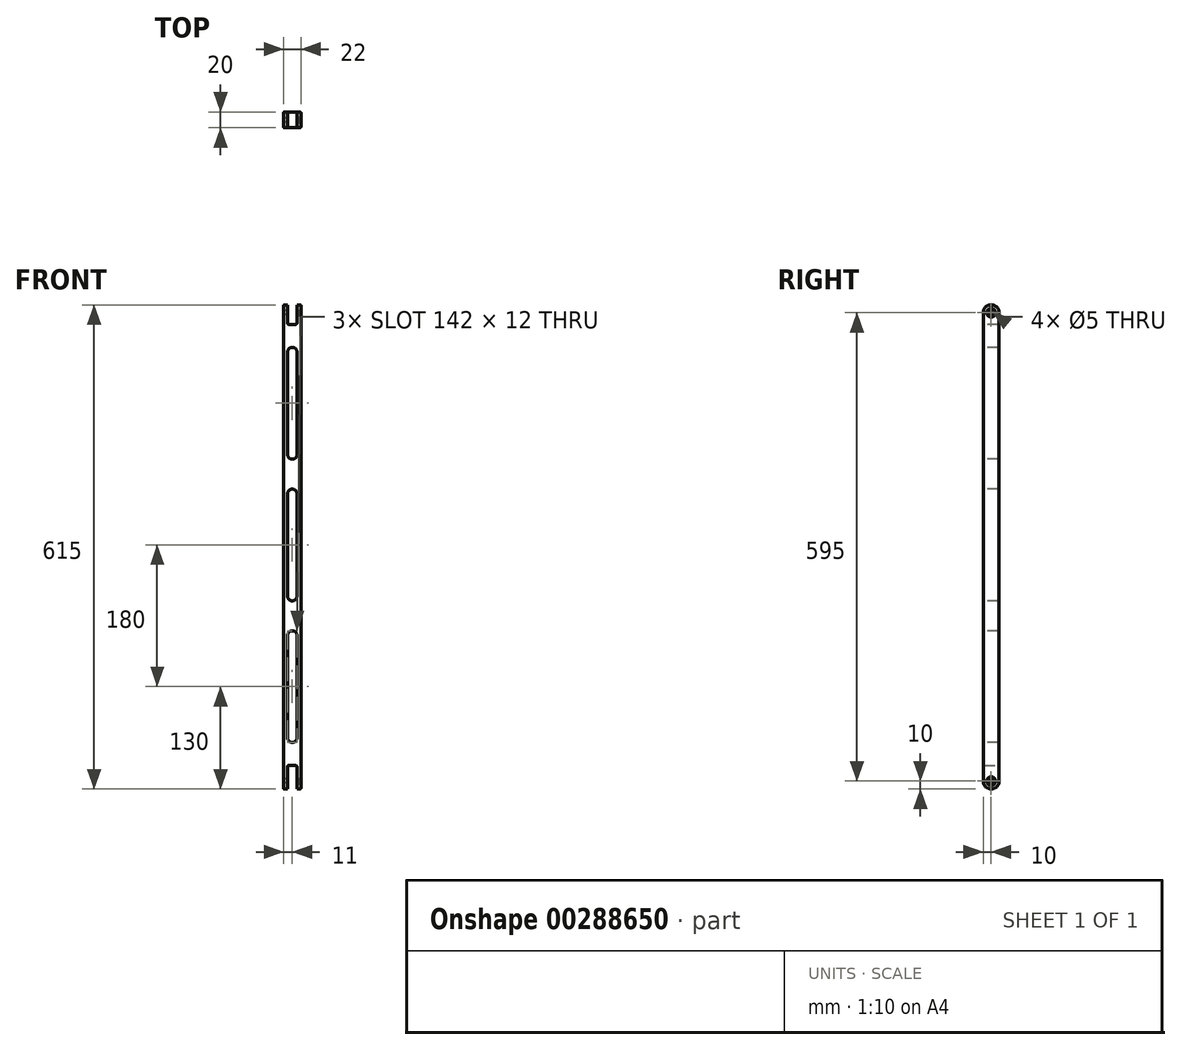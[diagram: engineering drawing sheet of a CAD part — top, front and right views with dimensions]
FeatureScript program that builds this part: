
annotation { "Feature Type Name" : "Feature", "Feature Type Description" : "" }
export const myFeature = defineFeature(function(context is Context, id is Id, definition is map)
    precondition{}
    {
        {
            var Q0;
            Q0=qCreatedBy(makeId("Front.planeOp"),FACE);
            var sketch = newSketch(context, id + "F0", { "sketchPlane" : qUnion([Q0])});
            skLineSegment(sketch, "E0.bottom", {"start": v(11, 307.5) * mm, "end": v(-11, 307.5) * mm});
            skLineSegment(sketch, "E0.top", {"start": v(11, -307.5) * mm, "end": v(-11, -307.5) * mm});
            skLineSegment(sketch, "E0.left", {"start": v(11, 307.5) * mm, "end": v(11, -307.5) * mm});
            skLineSegment(sketch, "E0.right", {"start": v(-11, 307.5) * mm, "end": v(-11, -307.5) * mm});
            skPoint(sketch, "E0.middle", {"position": v(0, 0) * mm});
            skSolve(sketch);
        }
        {
            var Q0;
            Q0=makeQuery(id+"F0.imprint","IMPRINT",FACE,{"disambiguationData":[TD([[makeQuery(id+"F0.imprint","IMPRINT",EDGE,{"derivedFrom":sQuery(id+"F0.wireOp",EDGE,"E0.bottom")}),1.0]])]});
            extrude(context, id + "F1", {"entities" : qUnion([Q0]), "depth" : 20 * mm});
        }
        {
            var Q0;
            Q0=makeQuery(id+"F1.opExtrude","SWEPT_FACE",FACE,{"disambiguationData":[OSD([sQuery(id+"F0.wireOp",EDGE,"E0.bottom")])]});
            var sketch = newSketch(context, id + "F2", { "sketchPlane" : qUnion([Q0])});
            skLineSegment(sketch, "E1.bottom", {"start": v(-6, 0) * mm, "end": v(6, 0) * mm});
            skLineSegment(sketch, "E1.top", {"start": v(-6, -20) * mm, "end": v(6, -20) * mm});
            skLineSegment(sketch, "E1.left", {"start": v(-6, 0) * mm, "end": v(-6, -20) * mm});
            skLineSegment(sketch, "E1.right", {"start": v(6, 0) * mm, "end": v(6, -20) * mm});
            skSolve(sketch);
        }
        {
            var Q0;
            Q0=makeQuery(id+"F2.imprint","IMPRINT",FACE,{"disambiguationData":[TD([[makeQuery(id+"F2.imprint","IMPRINT",EDGE,{"derivedFrom":sQuery(id+"F2.wireOp",EDGE,"E1.bottom")}),1.0]])]});
            extrude(context, id + "F3", {"entities" : qUnion([Q0]), "operationType" : NewBodyOperationType.REMOVE, "oppositeDirection" : true, "depth" : 25 * mm});
        }
        {
            var Q0;
            Q0=makeQuery(id+"F1.opExtrude","SWEPT_FACE",FACE,{"disambiguationData":[OSD([sQuery(id+"F0.wireOp",EDGE,"E0.top")])]});
            var sketch = newSketch(context, id + "F4", { "sketchPlane" : qUnion([Q0])});
            skLineSegment(sketch, "E2.bottom", {"start": v(-6, 20) * mm, "end": v(6, 20) * mm});
            skLineSegment(sketch, "E2.top", {"start": v(-6, 0) * mm, "end": v(6, 0) * mm});
            skLineSegment(sketch, "E2.left", {"start": v(-6, 20) * mm, "end": v(-6, 0) * mm});
            skLineSegment(sketch, "E2.right", {"start": v(6, 20) * mm, "end": v(6, 0) * mm});
            skSolve(sketch);
        }
        {
            var Q0;
            Q0=makeQuery(id+"F4.imprint","IMPRINT",FACE,{"disambiguationData":[TD([[makeQuery(id+"F4.imprint","IMPRINT",EDGE,{"derivedFrom":sQuery(id+"F4.wireOp",EDGE,"E2.bottom")}),1.0]])]});
            extrude(context, id + "F5", {"entities" : qUnion([Q0]), "operationType" : NewBodyOperationType.REMOVE, "oppositeDirection" : true, "depth" : 30 * mm});
        }
        {
            var Q0;
            {var subQ0=sQuery(id+"F0.wireOp",EDGE,"E0.right");var subQ1=sQuery(id+"F0.wireOp",EDGE,"E0.top");Q0=makeQuery(id+"F5.boolean.opBoolean","SPLIT",EDGE,{"disambiguationData":[TD([makeQuery(id+"F1.opExtrude","SWEPT_FACE",FACE,{"disambiguationData":[OSD([subQ0])]})])],"derivedFrom":makeQuery(id+"F1.opExtrude","CAP_EDGE",EDGE,{"disambiguationData":[OSD([subQ1])],"isStart":true})});}
            var Q1;
            {var subQ0=sQuery(id+"F0.wireOp",EDGE,"E0.left");var subQ1=sQuery(id+"F0.wireOp",EDGE,"E0.top");Q1=makeQuery(id+"F5.boolean.opBoolean","SPLIT",EDGE,{"disambiguationData":[TD([makeQuery(id+"F1.opExtrude","SWEPT_FACE",FACE,{"disambiguationData":[OSD([subQ0])]})])],"derivedFrom":makeQuery(id+"F1.opExtrude","CAP_EDGE",EDGE,{"disambiguationData":[OSD([subQ1])],"isStart":true})});}
            var Q2;
            {var subQ0=sQuery(id+"F0.wireOp",EDGE,"E0.left");var subQ1=sQuery(id+"F0.wireOp",EDGE,"E0.top");Q2=makeQuery(id+"F5.boolean.opBoolean","SPLIT",EDGE,{"disambiguationData":[TD([makeQuery(id+"F1.opExtrude","SWEPT_FACE",FACE,{"disambiguationData":[OSD([subQ0])]})])],"derivedFrom":makeQuery(id+"F1.opExtrude","CAP_EDGE",EDGE,{"disambiguationData":[OSD([subQ1])],"isStart":false})});}
            var Q3;
            {var subQ0=sQuery(id+"F0.wireOp",EDGE,"E0.right");var subQ1=sQuery(id+"F0.wireOp",EDGE,"E0.top");Q3=makeQuery(id+"F5.boolean.opBoolean","SPLIT",EDGE,{"disambiguationData":[TD([makeQuery(id+"F1.opExtrude","SWEPT_FACE",FACE,{"disambiguationData":[OSD([subQ0])]})])],"derivedFrom":makeQuery(id+"F1.opExtrude","CAP_EDGE",EDGE,{"disambiguationData":[OSD([subQ1])],"isStart":false})});}
            var Q4;
            {var subQ0=sQuery(id+"F0.wireOp",EDGE,"E0.bottom");var subQ1=sQuery(id+"F0.wireOp",EDGE,"E0.right");Q4=makeQuery(id+"F3.boolean.opBoolean","SPLIT",EDGE,{"disambiguationData":[TD([makeQuery(id+"F1.opExtrude","SWEPT_FACE",FACE,{"disambiguationData":[OSD([subQ1])]})])],"derivedFrom":makeQuery(id+"F1.opExtrude","CAP_EDGE",EDGE,{"disambiguationData":[OSD([subQ0])],"isStart":false})});}
            var Q5;
            {var subQ0=sQuery(id+"F0.wireOp",EDGE,"E0.bottom");var subQ1=sQuery(id+"F0.wireOp",EDGE,"E0.right");Q5=makeQuery(id+"F3.boolean.opBoolean","SPLIT",EDGE,{"disambiguationData":[TD([makeQuery(id+"F1.opExtrude","SWEPT_FACE",FACE,{"disambiguationData":[OSD([subQ1])]})])],"derivedFrom":makeQuery(id+"F1.opExtrude","CAP_EDGE",EDGE,{"disambiguationData":[OSD([subQ0])],"isStart":true})});}
            var Q6;
            {var subQ0=sQuery(id+"F0.wireOp",EDGE,"E0.bottom");var subQ1=sQuery(id+"F0.wireOp",EDGE,"E0.left");Q6=makeQuery(id+"F3.boolean.opBoolean","SPLIT",EDGE,{"disambiguationData":[TD([makeQuery(id+"F1.opExtrude","SWEPT_FACE",FACE,{"disambiguationData":[OSD([subQ1])]})])],"derivedFrom":makeQuery(id+"F1.opExtrude","CAP_EDGE",EDGE,{"disambiguationData":[OSD([subQ0])],"isStart":true})});}
            var Q7;
            {var subQ0=sQuery(id+"F0.wireOp",EDGE,"E0.bottom");var subQ1=sQuery(id+"F0.wireOp",EDGE,"E0.left");Q7=makeQuery(id+"F3.boolean.opBoolean","SPLIT",EDGE,{"disambiguationData":[TD([makeQuery(id+"F1.opExtrude","SWEPT_FACE",FACE,{"disambiguationData":[OSD([subQ1])]})])],"derivedFrom":makeQuery(id+"F1.opExtrude","CAP_EDGE",EDGE,{"disambiguationData":[OSD([subQ0])],"isStart":false})});}
            fillet(context, id + "F6", {"entities" : qUnion([Q0, Q1, Q2, Q3, Q4, Q5, Q6, Q7]), "radius" : 10 * mm, "tangentPropagation" : true, "allowEdgeOverflow" : false});
        }
        {
            var Q0;
            Q0=makeQuery(id+"F1.opExtrude","SWEPT_FACE",FACE,{"disambiguationData":[OSD([sQuery(id+"F0.wireOp",EDGE,"E0.right")])]});
            var sketch = newSketch(context, id + "F7", { "sketchPlane" : qUnion([Q0])});
            skCircle(sketch, "E3", {"center": v(10, 297.5) * mm, "radius": 2.5 * mm});
            skCircle(sketch, "E4", {"center": v(10, -297.5) * mm, "radius": 2.5 * mm});
            skSolve(sketch);
        }
        {
            var Q0;
            Q0=qSketchRegion(id+"F7",true);
            extrude(context, id + "F8", {"entities" : qUnion([Q0]), "operationType" : NewBodyOperationType.REMOVE, "oppositeDirection" : true, "depth" : 30 * mm});
        }
        {
            var Q0;
            Q0=makeQuery(id+"F1.opExtrude","CAP_FACE",FACE,{"disambiguationData":[OSD([sQuery(id+"F0.wireOp",EDGE,"E0.bottom"),sQuery(id+"F0.wireOp",EDGE,"E0.top"),sQuery(id+"F0.wireOp",EDGE,"E0.left"),sQuery(id+"F0.wireOp",EDGE,"E0.right")])],"isStart":false});
            var sketch = newSketch(context, id + "F9", { "sketchPlane" : qUnion([Q0])});
            skLineSegment(sketch, "E5.left", {"start": v(-6, -242.5) * mm, "end": v(-6, -112.5) * mm});
            skLineSegment(sketch, "E5.right", {"start": v(6, -242.5) * mm, "end": v(6, -112.5) * mm});
            skLineSegment(sketch, "E6.left", {"start": v(6, -62.5) * mm, "end": v(6, 67.5) * mm});
            skLineSegment(sketch, "E6.right", {"start": v(-6, -62.5) * mm, "end": v(-6, 67.5) * mm});
            skLineSegment(sketch, "E7.left", {"start": v(-6, 247.5) * mm, "end": v(-6, 117.5) * mm});
            skLineSegment(sketch, "E7.right", {"start": v(6, 247.5) * mm, "end": v(6, 117.5) * mm});
            skArc(sketch, "E8", {"start": v(6, -242.5) * mm, "mid": v(0, -248.5) * mm, "end": v(-6, -242.5) * mm});
            skArc(sketch, "E9", {"start": v(6, -112.5) * mm, "mid": v(0, -106.5) * mm, "end": v(-6, -112.5) * mm});
            skArc(sketch, "E10", {"start": v(-6, -62.5) * mm, "mid": v(0, -68.5) * mm, "end": v(6, -62.5) * mm});
            skArc(sketch, "E11", {"start": v(-6, 67.5) * mm, "mid": v(0, 73.5) * mm, "end": v(6, 67.5) * mm});
            skArc(sketch, "E12", {"start": v(-6, 117.5) * mm, "mid": v(0, 111.5) * mm, "end": v(6, 117.5) * mm});
            skArc(sketch, "E13", {"start": v(-6, 247.5) * mm, "mid": v(0, 253.5) * mm, "end": v(6, 247.5) * mm});
            skSolve(sketch);
        }
        {
            var Q0;
            Q0=makeQuery(id+"F9.imprint","IMPRINT",FACE,{"disambiguationData":[TD([[makeQuery(id+"F9.imprint","IMPRINT",EDGE,{"derivedFrom":sQuery(id+"F9.wireOp",EDGE,"E7.left")}),1.0]])]});
            var Q1;
            Q1=makeQuery(id+"F9.imprint","IMPRINT",FACE,{"disambiguationData":[TD([[makeQuery(id+"F9.imprint","IMPRINT",EDGE,{"derivedFrom":sQuery(id+"F9.wireOp",EDGE,"E6.left")}),1.0]])]});
            var Q2;
            Q2=makeQuery(id+"F9.imprint","IMPRINT",FACE,{"disambiguationData":[TD([[makeQuery(id+"F9.imprint","IMPRINT",EDGE,{"derivedFrom":sQuery(id+"F9.wireOp",EDGE,"E5.left")}),-1.0]])]});
            extrude(context, id + "F10", {"entities" : qUnion([Q0, Q1, Q2]), "operationType" : NewBodyOperationType.REMOVE, "oppositeDirection" : true, "depth" : 25 * mm, "offsetDistance" : 25 * mm});
        }
        {
            var Q0;
            Q0=makeQuery(id+"F1.opExtrude","CAP_EDGE",EDGE,{"disambiguationData":[OSD([sQuery(id+"F0.wireOp",EDGE,"E0.left")])],"isStart":true});
            var Q1;
            Q1=makeQuery(id+"F1.opExtrude","CAP_EDGE",EDGE,{"disambiguationData":[OSD([sQuery(id+"F0.wireOp",EDGE,"E0.right")])],"isStart":true});
            fillet(context, id + "F11", {"entities" : qUnion([Q0, Q1]), "radius" : 1 * mm, "tangentPropagation" : true, "allowEdgeOverflow" : false});
        }
        {
            var Q0;
            Q0=makeQuery(id+"F8.boolean.opBoolean","INTERSECT",EDGE,{"derivedFrom":[makeQuery(id+"F1.opExtrude","SWEPT_FACE",FACE,{"disambiguationData":[OSD([sQuery(id+"F0.wireOp",EDGE,"E0.left")])]}),makeQuery(id+"F8.opExtrude","SWEPT_FACE",FACE,{"disambiguationData":[OSD([sQuery(id+"F7.wireOp",EDGE,"E3")])]})]});
            var Q1;
            Q1=makeQuery(id+"F8.boolean.opBoolean","INTERSECT",EDGE,{"derivedFrom":[makeQuery(id+"F1.opExtrude","SWEPT_FACE",FACE,{"disambiguationData":[OSD([sQuery(id+"F0.wireOp",EDGE,"E0.left")])]}),makeQuery(id+"F8.opExtrude","SWEPT_FACE",FACE,{"disambiguationData":[OSD([sQuery(id+"F7.wireOp",EDGE,"E4")])]})]});
            chamfer(context, id + "F12", {"entities" : qUnion([Q0, Q1]), "width" : 3 * mm, "tangentPropagation" : true});
        }
        {
            var Q0;
            Q0=makeQuery(id+"F5.boolean.opBoolean","COPY",EDGE,{"derivedFrom":makeQuery(id+"F5.opExtrude","CAP_EDGE",EDGE,{"disambiguationData":[OSD([sQuery(id+"F4.wireOp",EDGE,"E2.left")])],"isStart":false})});
            var Q1;
            Q1=makeQuery(id+"F5.boolean.opBoolean","COPY",EDGE,{"derivedFrom":makeQuery(id+"F5.opExtrude","CAP_EDGE",EDGE,{"disambiguationData":[OSD([sQuery(id+"F4.wireOp",EDGE,"E2.right")])],"isStart":false})});
            var Q2;
            Q2=makeQuery(id+"F3.boolean.opBoolean","COPY",EDGE,{"derivedFrom":makeQuery(id+"F3.opExtrude","CAP_EDGE",EDGE,{"disambiguationData":[OSD([sQuery(id+"F2.wireOp",EDGE,"E1.right")])],"isStart":false})});
            var Q3;
            Q3=makeQuery(id+"F3.boolean.opBoolean","COPY",EDGE,{"derivedFrom":makeQuery(id+"F3.opExtrude","CAP_EDGE",EDGE,{"disambiguationData":[OSD([sQuery(id+"F2.wireOp",EDGE,"E1.left")])],"isStart":false})});
            fillet(context, id + "F13", {"entities" : qUnion([Q0, Q1, Q2, Q3]), "radius" : 2 * mm, "tangentPropagation" : true, "allowEdgeOverflow" : false});
        }
    });
